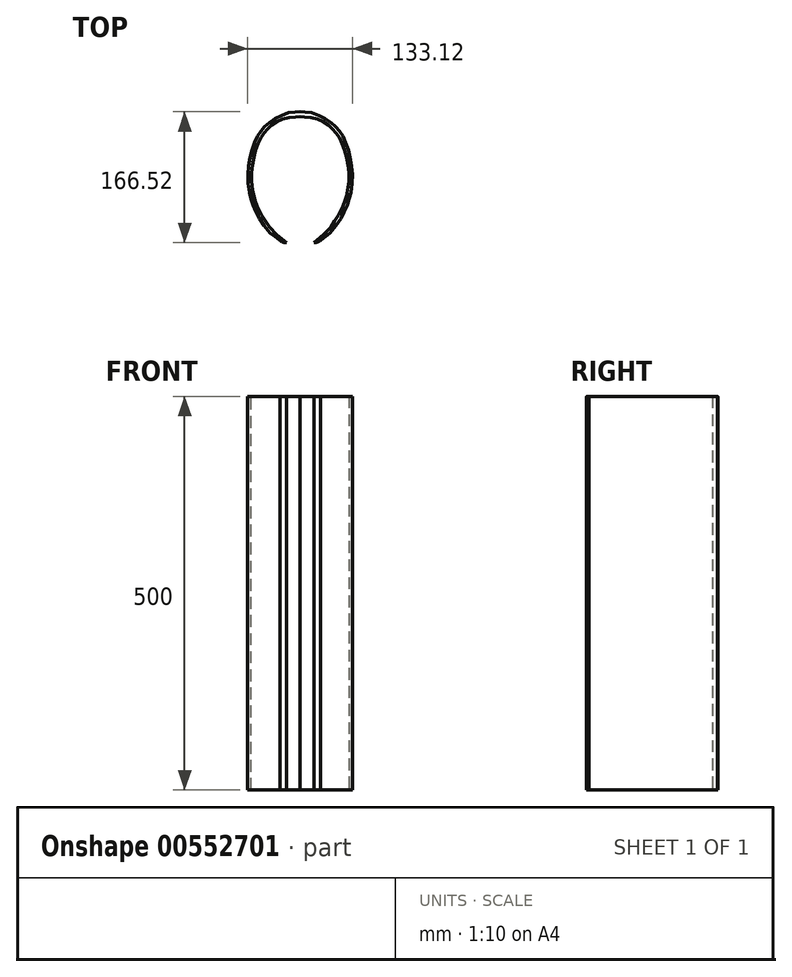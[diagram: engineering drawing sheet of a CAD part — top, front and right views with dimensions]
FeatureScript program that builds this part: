
annotation { "Feature Type Name" : "Feature", "Feature Type Description" : "" }
export const myFeature = defineFeature(function(context is Context, id is Id, definition is map)
    precondition{}
    {
        {
            var Q0;
            Q0=qCreatedBy(makeId("Top.planeOp"),FACE);
            var sketch = newSketch(context, id + "F0", { "sketchPlane" : qUnion([Q0])});
            skLineSegment(sketch, "E0", {"start": v(0, 0) * mm, "end": v(0, 21.59) * mm});
            skSolve(sketch);
        }
        {
            var Q0;
            Q0=qCreatedBy(makeId("Top.planeOp"),FACE);
            var sketch = newSketch(context, id + "F1", { "sketchPlane" : qUnion([Q0])});
            skLineSegment(sketch, "E1", {"start": v(0, 0) * mm, "end": v(0, -3.81) * mm});
            skSolve(sketch);
        }
        {
            var Q0;
            Q0=qCreatedBy(makeId("Top.planeOp"),FACE);
            var sketch = newSketch(context, id + "F2", { "sketchPlane" : qUnion([Q0])});
            skCircle(sketch, "E2", {"center": v(0, -3.81) * mm, "radius": 81.38 * mm});
            skSolve(sketch);
        }
        {
            var Q0;
            Q0=qCreatedBy(makeId("Top.planeOp"),FACE);
            var sketch = newSketch(context, id + "F3", { "sketchPlane" : qUnion([Q0])});
            skCircle(sketch, "E3", {"center": v(0, 21.59) * mm, "radius": 62.23 * mm});
            skSolve(sketch);
        }
        {
            var Q0;
            Q0=qCreatedBy(makeId("Top.planeOp"),FACE);
            var sketch = newSketch(context, id + "F4", { "sketchPlane" : qUnion([Q0])});
            skLineSegment(sketch, "E4", {"start": v(0, 0) * mm, "end": v(-33.02, 0) * mm});
            skSolve(sketch);
        }
        {
            var Q0;
            Q0=qCreatedBy(makeId("Top.planeOp"),FACE);
            var sketch = newSketch(context, id + "F5", { "sketchPlane" : qUnion([Q0])});
            skCircle(sketch, "E5", {"center": v(-33.02, 0) * mm, "radius": 99.06 * mm});
            skSolve(sketch);
        }
        {
            var Q0;
            Q0=qCreatedBy(makeId("Top.planeOp"),FACE);
            var sketch = newSketch(context, id + "F6", { "sketchPlane" : qUnion([Q0])});
            skLineSegment(sketch, "E6", {"start": v(0, 0) * mm, "end": v(-52.7, 0) * mm});
            skSolve(sketch);
        }
        {
            var Q0;
            Q0=qCreatedBy(makeId("Top.planeOp"),FACE);
            var sketch = newSketch(context, id + "F7", { "sketchPlane" : qUnion([Q0])});
            skLineSegment(sketch, "E7", {"start": v(-52.7, 0) * mm, "end": v(-52.7, 0.86) * mm});
            skSolve(sketch);
        }
        {
            var Q0;
            Q0=qCreatedBy(makeId("Top.planeOp"),FACE);
            var sketch = newSketch(context, id + "F8", { "sketchPlane" : qUnion([Q0])});
            skPoint(sketch, "E8", {"position": v(0, -82.55) * mm});
            skSolve(sketch);
        }
        {
            var Q0;
            Q0=qCreatedBy(makeId("Top.planeOp"),FACE);
            var sketch = newSketch(context, id + "F9", { "sketchPlane" : qUnion([Q0])});
            skPoint(sketch, "E9", {"position": v(0, -57.99) * mm});
            skSolve(sketch);
        }
        {
            var Q0;
            Q0=qCreatedBy(makeId("Top.planeOp"),FACE);
            var sketch = newSketch(context, id + "F10", { "sketchPlane" : qUnion([Q0])});
            skPoint(sketch, "E10", {"position": v(0, -70.69) * mm});
            skSolve(sketch);
        }
        {
            var Q0;
            Q0=qCreatedBy(makeId("Top.planeOp"),FACE);
            var sketch = newSketch(context, id + "F11", { "sketchPlane" : qUnion([Q0])});
            skCircle(sketch, "E11", {"center": v(0, -70.69) * mm, "radius": 12.7 * mm});
            skSolve(sketch);
        }
        {
            var Q0;
            Q0=qCreatedBy(makeId("Top.planeOp"),FACE);
            var sketch = newSketch(context, id + "F12", { "sketchPlane" : qUnion([Q0])});
            skCircle(sketch, "E12", {"center": v(0, -70.69) * mm, "radius": 18.41 * mm});
            skSolve(sketch);
        }
        {
            var Q0;
            Q0=qCreatedBy(makeId("Top.planeOp"),FACE);
            var sketch = newSketch(context, id + "F13", { "sketchPlane" : qUnion([Q0])});
            skLineSegment(sketch, "E13.bottom", {"start": v(16.9, -82.55) * mm, "end": v(0, -82.55) * mm});
            skLineSegment(sketch, "E13.top", {"start": v(16.9, -67.31) * mm, "end": v(0, -67.31) * mm});
            skLineSegment(sketch, "E13.left", {"start": v(16.9, -82.55) * mm, "end": v(16.9, -67.31) * mm});
            skLineSegment(sketch, "E13.right", {"start": v(0, -82.55) * mm, "end": v(0, -67.31) * mm});
            skSolve(sketch);
        }
        {
            var Q0;
            Q0=qCreatedBy(makeId("Top.planeOp"),FACE);
            var sketch = newSketch(context, id + "F14", { "sketchPlane" : qUnion([Q0])});
            skCircle(sketch, "E14", {"center": v(16.9, -67.31) * mm, "radius": 15.25 * mm});
            skSolve(sketch);
        }
        {
            var Q0;
            Q0=qCreatedBy(makeId("Top.planeOp"),FACE);
            var sketch = newSketch(context, id + "F15", { "sketchPlane" : qUnion([Q0])});
            skArc(sketch, "E15", {"start": v(9.73, -62.52) * mm, "mid": v(5.37, -59.18) * mm, "end": v(0, -57.99) * mm});
            skSolve(sketch);
        }
        {
            var Q0;
            Q0=qCreatedBy(makeId("Top.planeOp"),FACE);
            var sketch = newSketch(context, id + "F16", { "sketchPlane" : qUnion([Q0])});
            skArc(sketch, "E16", {"start": v(14.1, -58.85) * mm, "mid": v(7.78, -54) * mm, "end": v(0, -52.27) * mm});
            skSolve(sketch);
        }
        {
            var Q0;
            Q0=qCreatedBy(makeId("Top.planeOp"),FACE);
            var sketch = newSketch(context, id + "F17", { "sketchPlane" : qUnion([Q0])});
            skLineSegment(sketch, "E17", {"start": v(14.1, -58.85) * mm, "end": v(26.5, -73.6) * mm});
            skSolve(sketch);
        }
        {
            var Q0;
            Q0=qCreatedBy(makeId("Top.planeOp"),FACE);
            var sketch = newSketch(context, id + "F18", { "sketchPlane" : qUnion([Q0])});
            skLineSegment(sketch, "E18", {"start": v(0, -57.99) * mm, "end": v(0, -52.27) * mm});
            skSolve(sketch);
        }
        {
            var Q0;
            Q0=qCreatedBy(makeId("Top.planeOp"),FACE);
            var sketch = newSketch(context, id + "F19", { "sketchPlane" : qUnion([Q0])});
            skLineSegment(sketch, "E19", {"start": v(9.73, -62.52) * mm, "end": v(21.92, -77.04) * mm});
            skSolve(sketch);
        }
        {
            var Q0;
            Q0=qCreatedBy(makeId("Top.planeOp"),FACE);
            var sketch = newSketch(context, id + "F20", { "sketchPlane" : qUnion([Q0])});
            skLineSegment(sketch, "E20.bottom", {"start": v(0, -82.55) * mm, "end": v(4.45, -82.55) * mm});
            skLineSegment(sketch, "E20.top", {"start": v(0, -78.74) * mm, "end": v(4.45, -78.74) * mm});
            skLineSegment(sketch, "E20.left", {"start": v(0, -82.55) * mm, "end": v(0, -78.74) * mm});
            skLineSegment(sketch, "E20.right", {"start": v(4.45, -82.55) * mm, "end": v(4.45, -78.74) * mm});
            skSolve(sketch);
        }
        {
            var Q0;
            Q0=qCreatedBy(makeId("Top.planeOp"),FACE);
            var sketch = newSketch(context, id + "F21", { "sketchPlane" : qUnion([Q0])});
            skLineSegment(sketch, "E21.bottom", {"start": v(4.45, -82.55) * mm, "end": v(16.9, -82.55) * mm});
            skLineSegment(sketch, "E21.top", {"start": v(4.44, -78.74) * mm, "end": v(16.9, -78.74) * mm});
            skLineSegment(sketch, "E21.left", {"start": v(4.45, -82.55) * mm, "end": v(4.45, -78.74) * mm});
            skLineSegment(sketch, "E21.right", {"start": v(16.9, -82.55) * mm, "end": v(16.9, -78.74) * mm});
            skSolve(sketch);
        }
        {
            var Q0;
            Q0=qCreatedBy(makeId("Top.planeOp"),FACE);
            var sketch = newSketch(context, id + "F22", { "sketchPlane" : qUnion([Q0])});
            skFitSpline(sketch, "E22", {"points": [v(16.9, -78.74) * mm, v(19.53, -78.58) * mm, v(21.01, -78.06) * mm, v(21.56, -77.46) * mm, v(21.59, -76.88) * mm, v(21.22, -76.21) * mm], "startDerivative": vector(9.4, 0.18) * mm, "endDerivative": vector(-2.58, 3.68) * mm});
            skSolve(sketch);
        }
        {
            var Q0;
            Q0=qCreatedBy(makeId("Top.planeOp"),FACE);
            var sketch = newSketch(context, id + "F23", { "sketchPlane" : qUnion([Q0])});
            skArc(sketch, "E23", {"start": v(16.9, -82.55) * mm, "mid": v(21.52, -81.83) * mm, "end": v(25.7, -79.74) * mm});
            skSolve(sketch);
        }
        {
            var Q0;
            Q0=qCreatedBy(makeId("Top.planeOp"),FACE);
            var sketch = newSketch(context, id + "F24", { "sketchPlane" : qUnion([Q0]), "disableImprinting" : false});
            skFitSpline(sketch, "E24", {"points": [v(0, 77.57) * mm, v(12.57, 76.51) * mm, v(22.8, 74.29) * mm, v(30.34, 70.68) * mm, v(37.98, 65) * mm, v(42.64, 60.38) * mm, v(46.96, 55.09) * mm, v(50.77, 49) * mm, v(54.7, 39.93) * mm, v(58.1, 28.34) * mm, v(60.6, 14.67) * mm, v(61.56, 0) * mm, v(59.92, -17.09) * mm, v(58.1, -25.42) * mm, v(55.5, -33.24) * mm, v(50.47, -44.25) * mm, v(44.2, -54.46) * mm, v(35.28, -65.41) * mm, v(6.1, -88.1) * mm], "startDerivative": vector(209.38, 4.43) * mm, "endDerivative": vector(-215.1, -81.27) * mm});
            skSolve(sketch);
        }
        {
            var Q0;
            Q0=qCreatedBy(makeId("Top.planeOp"),FACE);
            var sketch = newSketch(context, id + "F25", { "sketchPlane" : qUnion([Q0]), "disableImprinting" : false});
            skFitSpline(sketch, "E25", {"points": [v(0, 83.98) * mm, v(12.76, 82.47) * mm, v(24.04, 78.94) * mm, v(32.9, 74.37) * mm, v(40.92, 68.43) * mm, v(46.01, 63.6) * mm, v(50.74, 57.69) * mm, v(54.75, 51.36) * mm, v(58.95, 41.5) * mm, v(62.66, 28.75) * mm, v(65.09, 14.53) * mm, v(66.02, 0) * mm, v(64.36, -17.78) * mm, v(62.22, -27.06) * mm, v(59.52, -35.2) * mm, v(54.69, -45.76) * mm, v(48.83, -55.68) * mm, v(38.54, -68.54) * mm, v(25.7, -79.74) * mm], "startDerivative": vector(236.92, 0.9) * mm, "endDerivative": vector(-291.13, -228.04) * mm});
            skSolve(sketch);
        }
        {
            var Q0;
            Q0=qCreatedBy(makeId("Top.planeOp"),FACE);
            var sketch = newSketch(context, id + "F26", { "sketchPlane" : qUnion([Q0])});
            skPoint(sketch, "E26", {"position": v(6.99, -80.01) * mm});
            skSolve(sketch);
        }
        {
            var Q0;
            Q0=qCreatedBy(makeId("Top.planeOp"),FACE);
            var sketch = newSketch(context, id + "F27", { "sketchPlane" : qUnion([Q0])});
            skArc(sketch, "E27", {"start": v(6.99, -82.55) * mm, "mid": v(5.19, -81.8) * mm, "end": v(4.45, -80.01) * mm});
            skSolve(sketch);
        }
        {
            var Q0;
            Q0=qCreatedBy(makeId("Top.planeOp"),FACE);
            var sketch = newSketch(context, id + "F28", { "sketchPlane" : qUnion([Q0])});
            skArc(sketch, "E28", {"start": v(4.45, -80.01) * mm, "mid": v(6.33, -77.56) * mm, "end": v(9.18, -78.74) * mm});
            skSolve(sketch);
        }
        {
            var Q0;
            Q0=qCreatedBy(makeId("Top.planeOp"),FACE);
            var sketch = newSketch(context, id + "F29", { "sketchPlane" : qUnion([Q0])});
            skPoint(sketch, "E29", {"position": v(66.04, 0) * mm});
            skSolve(sketch);
        }
        {
            var Q0;
            Q0=qCreatedBy(makeId("Top.planeOp"),FACE);
            var sketch = newSketch(context, id + "F30", { "sketchPlane" : qUnion([Q0])});
            skPoint(sketch, "E30", {"position": v(59.82, 0) * mm});
            skSolve(sketch);
        }
        {
            var Q0;
            Q0=qCreatedBy(makeId("Top.planeOp"),FACE);
            var sketch = newSketch(context, id + "F31", { "sketchPlane" : qUnion([Q0])});
            skLineSegment(sketch, "E31", {"start": v(59.82, 19.76) * mm, "end": v(59.82, -17.73) * mm});
            skSolve(sketch);
        }
        {
            var Q0;
            Q0=qCreatedBy(makeId("Top.planeOp"),FACE);
            var sketch = newSketch(context, id + "F32", { "sketchPlane" : qUnion([Q0])});
            skLineSegment(sketch, "E32", {"start": v(0, 83.98) * mm, "end": v(0, 77.57) * mm});
            skSolve(sketch);
        }
        {
            var Q0;
            Q0=qCreatedBy(makeId("Top.planeOp"),FACE);
            var sketch = newSketch(context, id + "F33", { "sketchPlane" : qUnion([Q0])});
            skLineSegment(sketch, "E33", {"start": v(16.9, -78.74) * mm, "end": v(9.18, -78.74) * mm});
            skSolve(sketch);
        }
        {
            var Q0;
            Q0=qCreatedBy(makeId("Top.planeOp"),FACE);
            var sketch = newSketch(context, id + "F34", { "sketchPlane" : qUnion([Q0])});
            skLineSegment(sketch, "E34", {"start": v(6.99, -82.55) * mm, "end": v(16.9, -82.55) * mm});
            skSolve(sketch);
        }
        {
            var Q0;
            Q0=qCreatedBy(makeId("Top.planeOp"),FACE);
            var sketch = newSketch(context, id + "F35", { "sketchPlane" : qUnion([Q0])});
            skLineSegment(sketch, "E35.0", {"start": v(59.82, 19.76) * mm, "end": v(59.82, -17.73) * mm});
            skFitSpline(sketch, "E36.0", {"points": [v(0, 77.57) * mm, v(4.14, 77.4) * mm, v(13.21, 76.73) * mm, v(22.82, 74.63) * mm, v(30.4, 71) * mm, v(38.1, 65.13) * mm, v(42.63, 60.51) * mm, v(47.14, 55.07) * mm, v(51.01, 49.01) * mm, v(54.98, 39.77) * mm, v(58.34, 28.32) * mm, v(60.83, 14.44) * mm, v(62.12, 0.33) * mm, v(60.18, -16.97) * mm, v(58.24, -25.32) * mm, v(55.6, -33.45) * mm, v(50.74, -44.44) * mm, v(43.82, -55.12) * mm, v(36.71, -65.37) * mm, v(13.21, -85.42) * mm, v(6.13, -88.1) * mm]});
            skLineSegment(sketch, "E37.0", {"start": v(0, 83.98) * mm, "end": v(0, 77.57) * mm});
            skFitSpline(sketch, "E38.0", {"points": [v(0, 83.98) * mm, v(4.87, 83.4) * mm, v(12.49, 83.1) * mm, v(24.17, 79.16) * mm, v(32.9, 74.75) * mm, v(40.99, 68.54) * mm, v(46.08, 63.8) * mm, v(50.89, 57.63) * mm, v(55.07, 51.39) * mm, v(59.24, 41.3) * mm, v(62.97, 28.78) * mm, v(65.27, 14.32) * mm, v(66.56, 0.3) * mm, v(64.71, -17.67) * mm, v(62.33, -26.94) * mm, v(59.72, -35.32) * mm, v(54.66, -46.12) * mm, v(49.25, -55.74) * mm, v(37.88, -69.94) * mm, v(32.25, -74.62) * mm, v(25.7, -79.74) * mm]});
            skArc(sketch, "E39.0", {"start": v(16.9, -82.55) * mm, "mid": v(21.52, -81.83) * mm, "end": v(25.7, -79.74) * mm});
            skLineSegment(sketch, "E40.0", {"start": v(6.99, -82.55) * mm, "end": v(16.9, -82.55) * mm});
            skArc(sketch, "E41.0", {"start": v(6.99, -82.55) * mm, "mid": v(5.19, -81.8) * mm, "end": v(4.45, -80.01) * mm});
            skArc(sketch, "E42.0", {"start": v(4.45, -80.01) * mm, "mid": v(6.33, -77.56) * mm, "end": v(9.18, -78.74) * mm});
            skLineSegment(sketch, "E43.0", {"start": v(16.9, -78.74) * mm, "end": v(9.18, -78.74) * mm});
            skFitSpline(sketch, "E44.0", {"points": [v(16.9, -78.74) * mm, v(17.83, -78.72) * mm, v(19.47, -78.71) * mm, v(21, -78.17) * mm, v(21.63, -77.5) * mm, v(21.65, -76.86) * mm, v(21.36, -76.4) * mm, v(21.22, -76.21) * mm]});
            skLineSegment(sketch, "E45.0", {"start": v(9.73, -62.52) * mm, "end": v(21.92, -77.04) * mm});
            skArc(sketch, "E46.0", {"start": v(9.73, -62.52) * mm, "mid": v(5.37, -59.18) * mm, "end": v(0, -57.99) * mm});
            skLineSegment(sketch, "E47.0", {"start": v(0, -57.99) * mm, "end": v(0, -52.27) * mm});
            skArc(sketch, "E48.0", {"start": v(14.1, -58.85) * mm, "mid": v(7.78, -54) * mm, "end": v(0, -52.27) * mm});
            skLineSegment(sketch, "E49.0", {"start": v(14.1, -58.85) * mm, "end": v(26.5, -73.6) * mm});
            skSolve(sketch);
        }
        {
            var Q0;
            Q0 = qSketchRegion(id + "F35", true);
            extrude(context, id + "F36", {"entities" : qUnion([Q0]), "depth" : 500 * mm, "offsetDistance" : 25.4 * mm, "symmetric" : true});
        }
        {
            var Q0;
            Q0=makeQuery(id+"F36.opExtrude","SWEPT_BODY",BODY,{"disambiguationData":[OSD([sQuery(id+"F35.wireOp",EDGE,"E35.0"),sQuery(id+"F35.wireOp",EDGE,"E36.0"),sQuery(id+"F35.wireOp",EDGE,"E37.0"),sQuery(id+"F35.wireOp",EDGE,"E38.0"),sQuery(id+"F35.wireOp",EDGE,"E39.0"),sQuery(id+"F35.wireOp",EDGE,"E40.0"),sQuery(id+"F35.wireOp",EDGE,"E41.0"),sQuery(id+"F35.wireOp",EDGE,"E42.0"),sQuery(id+"F35.wireOp",EDGE,"E43.0"),sQuery(id+"F35.wireOp",EDGE,"E44.0"),sQuery(id+"F35.wireOp",EDGE,"E45.0"),sQuery(id+"F35.wireOp",EDGE,"E46.0"),sQuery(id+"F35.wireOp",EDGE,"E47.0"),sQuery(id+"F35.wireOp",EDGE,"E48.0"),sQuery(id+"F35.wireOp",EDGE,"E49.0")])]});
            var Q1;
            Q1=qCreatedBy(makeId("Right.planeOp"),FACE);
            mirror(context, id + "F37", {"operationType" : NewBodyOperationType.ADD, "entities" : qUnion([Q0]), "mirrorPlane" : qUnion([Q1])});
        }
    });
